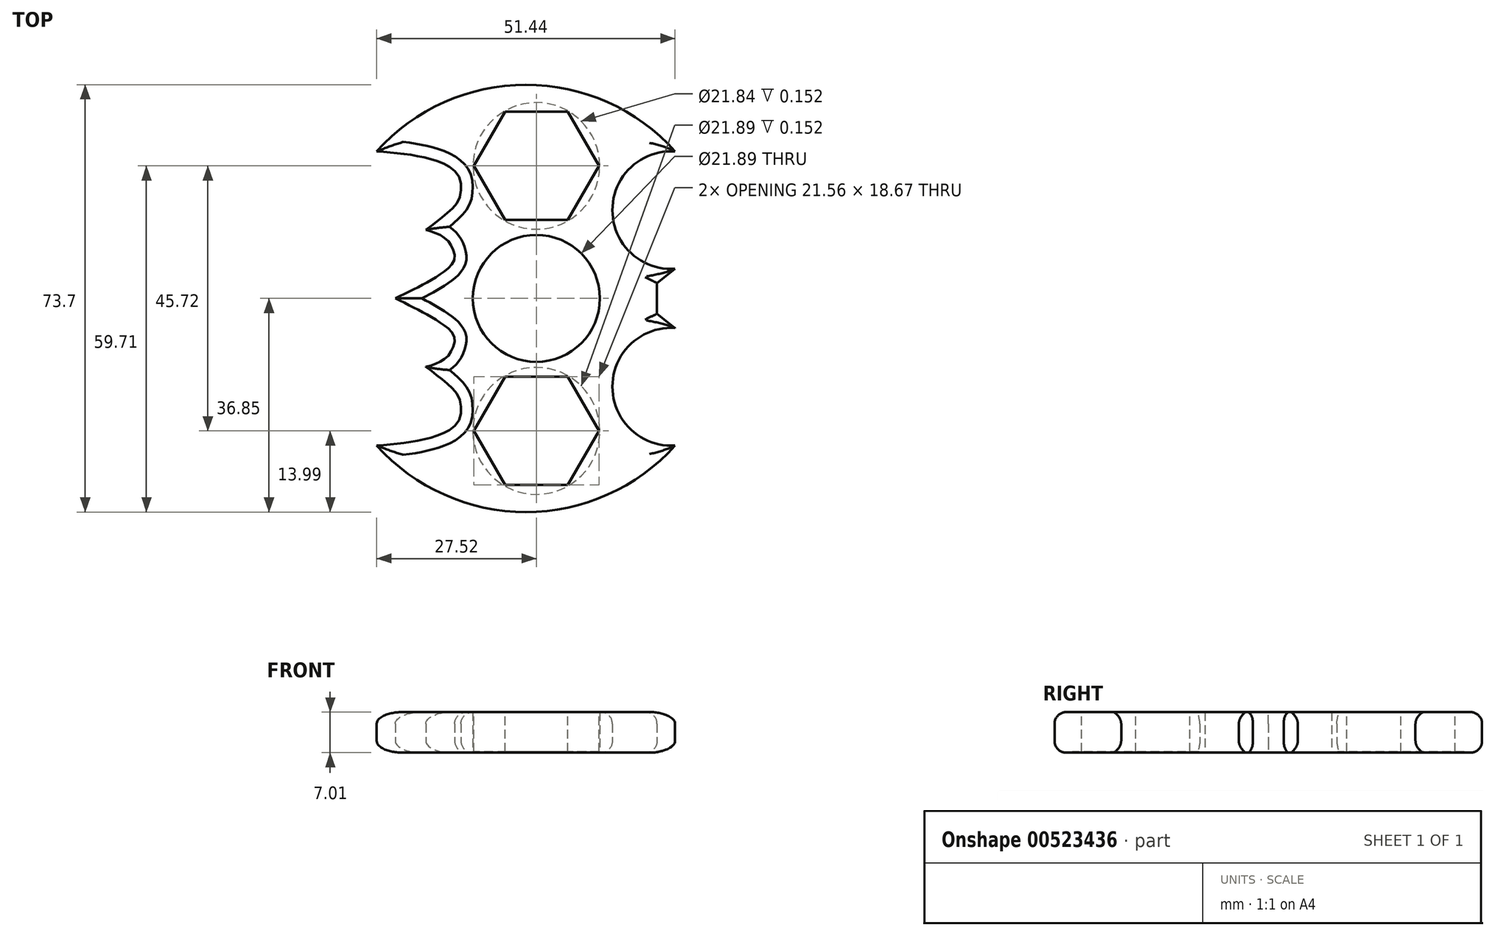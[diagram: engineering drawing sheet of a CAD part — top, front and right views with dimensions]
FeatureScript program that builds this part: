
annotation { "Feature Type Name" : "Feature", "Feature Type Description" : "" }
export const myFeature = defineFeature(function(context is Context, id is Id, definition is map)
    precondition{}
    {
        {
            var Q0;
            Q0=qCreatedBy(makeId("Top.planeOp"),FACE);
            var sketch = newSketch(context, id + "F0", { "sketchPlane" : qUnion([Q0])});
            skCircle(sketch, "E0.cCircle", {"center": v(0, 0) * mm, "radius": 12.7 * mm, "construction": true});
            skCircle(sketch, "E1", {"center": v(0, 0) * mm, "radius": 10.95 * mm});
            skLineSegment(sketch, "E2.bottom", {"start": v(4.8, 12.7) * mm, "end": v(-4.8, 12.7) * mm});
            skLineSegment(sketch, "E3.bottom", {"start": v(4.8, -11.43) * mm, "end": v(-4.8, -11.43) * mm});
            skLineSegment(sketch, "E4.MirrorCS", {"start": v(4.8, -76.2) * mm, "end": v(-4.8, -76.2) * mm});
            skLineSegment(sketch, "E5.MirrorCS", {"start": v(4.8, -73.66) * mm, "end": v(4.8, -76.2) * mm});
            skLineSegment(sketch, "E6.MirrorCS", {"start": v(7.33, -12.7) * mm, "end": v(-7.33, -12.7) * mm});
            skCircle(sketch, "E7.MirrorC", {"center": v(0, -22.86) * mm, "radius": 12.7 * mm, "construction": true});
            skCircle(sketch, "E8.MirrorC", {"center": v(0, -22.86) * mm, "radius": 10.95 * mm});
            skCircle(sketch, "E9.MirrorC", {"center": v(0, 22.86) * mm, "radius": 12.5 * mm, "construction": true});
            skCircle(sketch, "E10.MirrorC", {"center": v(0, 22.86) * mm, "radius": 10.92 * mm});
            skLineSegment(sketch, "E11", {"start": v(20.81, 0) * mm, "end": v(20.81, 2.65) * mm});
            skLineSegment(sketch, "E12", {"start": v(20.81, 2.65) * mm, "end": v(23.92, 5.09) * mm});
            skArc(sketch, "E13", {"start": v(23.92, 25.37) * mm, "mid": v(13.1, 15.23) * mm, "end": v(23.92, 5.09) * mm});
            skArc(sketch, "E14", {"start": v(23.92, 25.37) * mm, "mid": v(-1.8, 36.85) * mm, "end": v(-27.52, 25.37) * mm});
            skFitSpline(sketch, "E15", {"points": [v(-27.52, 25.37) * mm, v(-13.04, 18.5) * mm, v(-19.05, 11.82) * mm], "startDerivative": vector(78.47, -4.85) * mm, "endDerivative": vector(-39.75, -28.97) * mm});
            skFitSpline(sketch, "E16", {"points": [v(-19.05, 11.82) * mm, v(-14.33, 8.23) * mm, v(-24.33, 0) * mm], "startDerivative": vector(29.04, -7.57) * mm, "endDerivative": vector(-56.04, -26.66) * mm});
            skLineSegment(sketch, "E17.MirrorCS", {"start": v(20.81, 0) * mm, "end": v(20.81, -2.65) * mm});
            skLineSegment(sketch, "E18.MirrorCS", {"start": v(20.81, -2.65) * mm, "end": v(23.92, -5.09) * mm});
            skArc(sketch, "E19.MirrorCS", {"start": v(23.92, -25.37) * mm, "mid": v(13.1, -15.23) * mm, "end": v(23.92, -5.09) * mm});
            skArc(sketch, "E20.MirrorCS", {"start": v(23.92, -25.37) * mm, "mid": v(-1.8, -36.85) * mm, "end": v(-27.52, -25.37) * mm});
            skFitSpline(sketch, "E21.MirrorCS", {"points": [v(-27.52, -25.37) * mm, v(-13.04, -18.5) * mm, v(-19.05, -11.82) * mm], "startDerivative": vector(78.47, 4.85) * mm, "endDerivative": vector(-39.75, 28.97) * mm});
            skFitSpline(sketch, "E22.MirrorCS", {"points": [v(-19.05, -11.82) * mm, v(-14.33, -8.23) * mm, v(-24.33, 0) * mm], "startDerivative": vector(29.04, 7.57) * mm, "endDerivative": vector(-56.04, 26.66) * mm});
            skSolve(sketch);
        }
        {
            var Q0;
            Q0=qSketchRegion(id+"F0",true);
            var Q1;
            {var subQ1=sQuery(id+"F0.wireOp",EDGE,"E0.1");Q1=makeQuery(id+"F0.imprint","IMPRINT",FACE,{"disambiguationData":[TD([[makeQuery(id+"F0.imprint","IMPRINT",EDGE,{"derivedFrom":subQ1}),-1.0]])]});}
            extrude(context, id + "F1", {"entities" : qUnion([Q0, Q1]), "depth" : 7 * mm, "offsetDistance" : 25.4 * mm});
        }
        {
            var Q0;
            Q0=makeQuery(id+"F1.opExtrude","CAP_EDGE",EDGE,{"disambiguationData":[OSD([sQuery(id+"F0.wireOp",EDGE,"UyywlGDB-5Jgc-yo0l-qGuh-bbdJMILhEXu3")])],"isStart":true});
            var Q1;
            Q1=makeQuery(id+"F1.opExtrude","CAP_EDGE",EDGE,{"disambiguationData":[OSD([sQuery(id+"F0.wireOp",EDGE,"UyywlGDB-5Jgc-yo0l-qGuh-bbdJMILhEXu3")])],"isStart":false});
            var Q2;
            Q2=makeQuery(id+"F1.opExtrude","CAP_EDGE",EDGE,{"disambiguationData":[OSD([sQuery(id+"F0.wireOp",EDGE,"WgatU1v8-sKzI-u2eX-Sff9-52ynPzkIywBV")])],"isStart":true});
            var Q3;
            Q3=makeQuery(id+"F1.opExtrude","CAP_EDGE",EDGE,{"disambiguationData":[OSD([sQuery(id+"F0.wireOp",EDGE,"WgatU1v8-sKzI-u2eX-Sff9-52ynPzkIywBV")])],"isStart":false});
            var Q4;
            Q4=makeQuery(id+"F1.opExtrude","CAP_EDGE",EDGE,{"disambiguationData":[OSD([sQuery(id+"F0.wireOp",EDGE,"6KD2nS0l-Hg2D-HksP-1Ouw-CZn9uDxc5PTc")])],"isStart":true});
            var Q5;
            Q5=makeQuery(id+"F1.opExtrude","CAP_EDGE",EDGE,{"disambiguationData":[OSD([sQuery(id+"F0.wireOp",EDGE,"J5kapQ5n-iDyL-HHIj-PmFu-jLv0Z1pDbZps")])],"isStart":true});
            var Q6;
            Q6=makeQuery(id+"F1.opExtrude","CAP_EDGE",EDGE,{"disambiguationData":[OSD([sQuery(id+"F0.wireOp",EDGE,"J5kapQ5n-iDyL-HHIj-PmFu-jLv0Z1pDbZps")])],"isStart":false});
            var Q7;
            Q7=makeQuery(id+"F1.opExtrude","CAP_EDGE",EDGE,{"disambiguationData":[OSD([sQuery(id+"F0.wireOp",EDGE,"6KD2nS0l-Hg2D-HksP-1Ouw-CZn9uDxc5PTc")])],"isStart":false});
            var Q8;
            Q8=makeQuery(id+"F1.opExtrude","CAP_EDGE",EDGE,{"disambiguationData":[OSD([sQuery(id+"F0.wireOp",EDGE,"RGc6EknY-F7E9-4rBv-WTXc-wHNUPe1DTfrm")])],"isStart":true});
            var Q9;
            Q9=makeQuery(id+"F1.opExtrude","CAP_EDGE",EDGE,{"disambiguationData":[OSD([sQuery(id+"F0.wireOp",EDGE,"RGc6EknY-F7E9-4rBv-WTXc-wHNUPe1DTfrm")])],"isStart":false});
            var Q10;
            Q10=makeQuery(id+"F1.opExtrude","CAP_EDGE",EDGE,{"disambiguationData":[OSD([sQuery(id+"F0.wireOp",EDGE,"wNdpGod0-uiPN-bQcB-ljPU-xclPaN7TEj14")])],"isStart":false});
            var Q11;
            Q11=makeQuery(id+"F1.opExtrude","CAP_EDGE",EDGE,{"disambiguationData":[OSD([sQuery(id+"F0.wireOp",EDGE,"wNdpGod0-uiPN-bQcB-ljPU-xclPaN7TEj14")])],"isStart":true});
            var Q12;
            Q12=makeQuery(id+"F1.opExtrude","CAP_EDGE",EDGE,{"disambiguationData":[OSD([sQuery(id+"F0.wireOp",EDGE,"i4p45k76-JwoF-I5pY-E1qU-otX4NrZX3LmJ")])],"isStart":true});
            var Q13;
            Q13=makeQuery(id+"F1.opExtrude","CAP_EDGE",EDGE,{"disambiguationData":[OSD([sQuery(id+"F0.wireOp",EDGE,"i4p45k76-JwoF-I5pY-E1qU-otX4NrZX3LmJ")])],"isStart":false});
            var Q14;
            Q14=makeQuery(id+"F1.opExtrude","CAP_EDGE",EDGE,{"disambiguationData":[OSD([sQuery(id+"F0.wireOp",EDGE,"TCmziQ1A-WoUB-5TRC-2sz4-3Qv1A3Y1Nol2")])],"isStart":true});
            var Q15;
            Q15=makeQuery(id+"F1.opExtrude","CAP_EDGE",EDGE,{"disambiguationData":[OSD([sQuery(id+"F0.wireOp",EDGE,"TCmziQ1A-WoUB-5TRC-2sz4-3Qv1A3Y1Nol2")])],"isStart":false});
            var Q16;
            Q16=makeQuery(id+"F1.opExtrude","CAP_EDGE",EDGE,{"disambiguationData":[OSD([sQuery(id+"F0.wireOp",EDGE,"E14")])],"isStart":false});
            var Q17;
            Q17=makeQuery(id+"F1.opExtrude","CAP_EDGE",EDGE,{"disambiguationData":[OSD([sQuery(id+"F0.wireOp",EDGE,"E14")])],"isStart":true});
            var Q18;
            Q18=makeQuery(id+"F1.opExtrude","CAP_EDGE",EDGE,{"disambiguationData":[OSD([sQuery(id+"F0.wireOp",EDGE,"E20.MirrorCS")])],"isStart":true});
            var Q19;
            Q19=makeQuery(id+"F1.opExtrude","CAP_EDGE",EDGE,{"disambiguationData":[OSD([sQuery(id+"F0.wireOp",EDGE,"E20.MirrorCS")])],"isStart":false});
            var Q20;
            Q20=makeQuery(id+"F1.opExtrude","CAP_EDGE",EDGE,{"disambiguationData":[OSD([sQuery(id+"F0.wireOp",EDGE,"E19.MirrorCS")])],"isStart":false});
            var Q21;
            Q21=makeQuery(id+"F1.opExtrude","CAP_EDGE",EDGE,{"disambiguationData":[OSD([sQuery(id+"F0.wireOp",EDGE,"E13")])],"isStart":false});
            var Q22;
            Q22=makeQuery(id+"F1.opExtrude","CAP_EDGE",EDGE,{"disambiguationData":[OSD([sQuery(id+"F0.wireOp",EDGE,"E19.MirrorCS")])],"isStart":true});
            var Q23;
            Q23=makeQuery(id+"F1.opExtrude","CAP_EDGE",EDGE,{"disambiguationData":[OSD([sQuery(id+"F0.wireOp",EDGE,"E13")])],"isStart":true});
            var Q24;
            Q24=makeQuery(id+"F1.opExtrude","CAP_EDGE",EDGE,{"disambiguationData":[OSD([sQuery(id+"F0.wireOp",EDGE,"E11"),sQuery(id+"F0.wireOp",EDGE,"E17.MirrorCS")])],"isStart":true});
            var Q25;
            Q25=makeQuery(id+"F1.opExtrude","CAP_EDGE",EDGE,{"disambiguationData":[OSD([sQuery(id+"F0.wireOp",EDGE,"E11"),sQuery(id+"F0.wireOp",EDGE,"E17.MirrorCS")])],"isStart":false});
            var Q26;
            Q26=makeQuery(id+"F1.opExtrude","CAP_EDGE",EDGE,{"disambiguationData":[OSD([sQuery(id+"F0.wireOp",EDGE,"E12")])],"isStart":false});
            var Q27;
            Q27=makeQuery(id+"F1.opExtrude","CAP_EDGE",EDGE,{"disambiguationData":[OSD([sQuery(id+"F0.wireOp",EDGE,"E12")])],"isStart":true});
            var Q28;
            Q28=makeQuery(id+"F1.opExtrude","CAP_EDGE",EDGE,{"disambiguationData":[OSD([sQuery(id+"F0.wireOp",EDGE,"E18.MirrorCS")])],"isStart":false});
            var Q29;
            Q29=makeQuery(id+"F1.opExtrude","CAP_EDGE",EDGE,{"disambiguationData":[OSD([sQuery(id+"F0.wireOp",EDGE,"E18.MirrorCS")])],"isStart":true});
            var Q30;
            Q30=makeQuery(id+"F1.opExtrude","CAP_EDGE",EDGE,{"disambiguationData":[OSD([sQuery(id+"F0.wireOp",EDGE,"E21.MirrorCS")])],"isStart":false});
            var Q31;
            Q31=makeQuery(id+"F1.opExtrude","CAP_EDGE",EDGE,{"disambiguationData":[OSD([sQuery(id+"F0.wireOp",EDGE,"E22.MirrorCS")])],"isStart":false});
            var Q32;
            Q32=makeQuery(id+"F1.opExtrude","CAP_EDGE",EDGE,{"disambiguationData":[OSD([sQuery(id+"F0.wireOp",EDGE,"E16")])],"isStart":false});
            var Q33;
            Q33=makeQuery(id+"F1.opExtrude","CAP_EDGE",EDGE,{"disambiguationData":[OSD([sQuery(id+"F0.wireOp",EDGE,"E15")])],"isStart":false});
            var Q34;
            Q34=makeQuery(id+"F1.opExtrude","CAP_EDGE",EDGE,{"disambiguationData":[OSD([sQuery(id+"F0.wireOp",EDGE,"E15")])],"isStart":true});
            var Q35;
            Q35=makeQuery(id+"F1.opExtrude","CAP_EDGE",EDGE,{"disambiguationData":[OSD([sQuery(id+"F0.wireOp",EDGE,"E16")])],"isStart":true});
            var Q36;
            Q36=makeQuery(id+"F1.opExtrude","CAP_EDGE",EDGE,{"disambiguationData":[OSD([sQuery(id+"F0.wireOp",EDGE,"E22.MirrorCS")])],"isStart":true});
            var Q37;
            Q37=makeQuery(id+"F1.opExtrude","CAP_EDGE",EDGE,{"disambiguationData":[OSD([sQuery(id+"F0.wireOp",EDGE,"E21.MirrorCS")])],"isStart":true});
            fillet(context, id + "F2", {"entities" : qUnion([Q0, Q1, Q2, Q3, Q4, Q5, Q6, Q7, Q8, Q9, Q10, Q11, Q12, Q13, Q14, Q15, Q16, Q17, Q18, Q19, Q20, Q21, Q22, Q23, Q24, Q25, Q26, Q27, Q28, Q29, Q30, Q31, Q32, Q33, Q34, Q35, Q36, Q37]), "radius" : 2.03 * mm, "tangentPropagation" : true, "allowEdgeOverflow" : false});
        }
        {
            var Q0;
            Q0=makeQuery(id+"F1.opExtrude","CAP_FACE",FACE,{"disambiguationData":[OSD([sQuery(id+"F0.wireOp",EDGE,"E1"),sQuery(id+"F0.wireOp",EDGE,"514edc31-06ac-40e3-995b-7c1c53eea3582.MirrorCS"),sQuery(id+"F0.wireOp",EDGE,"E8.MirrorC"),sQuery(id+"F0.wireOp",EDGE,"514edc31-06ac-40e3-995b-7c1c53eea3586.MirrorCS"),sQuery(id+"F0.wireOp",EDGE,"5bda6188-825b-4b41-803b-8e19fa25ede90.MirrorCS"),sQuery(id+"F0.wireOp",EDGE,"455845eb-5c42-433d-a614-b21934a475661.MirrorCS"),sQuery(id+"F0.wireOp",EDGE,"455845eb-5c42-433d-a614-b21934a475662.MirrorCS"),sQuery(id+"F0.wireOp",EDGE,"E10.MirrorC"),sQuery(id+"F0.wireOp",EDGE,"QdPQ0PJ2-Wn2Q-TIlk-QB5f-A208rq11A3H9"),sQuery(id+"F0.wireOp",EDGE,"UyywlGDB-5Jgc-yo0l-qGuh-bbdJMILhEXu3"),sQuery(id+"F0.wireOp",EDGE,"WgatU1v8-sKzI-u2eX-Sff9-52ynPzkIywBV"),sQuery(id+"F0.wireOp",EDGE,"6KD2nS0l-Hg2D-HksP-1Ouw-CZn9uDxc5PTc"),sQuery(id+"F0.wireOp",EDGE,"J5kapQ5n-iDyL-HHIj-PmFu-jLv0Z1pDbZps")])],"isStart":false});
            var sketch = newSketch(context, id + "F3", { "sketchPlane" : qUnion([Q0])});
            skCircle(sketch, "E23.cCircle", {"center": v(0, -22.86) * mm, "radius": 9.33 * mm, "construction": true});
            skLineSegment(sketch, "E23.0", {"start": v(-5.39, -13.53) * mm, "end": v(5.39, -13.53) * mm});
            skLineSegment(sketch, "E23.1", {"start": v(5.39, -13.53) * mm, "end": v(10.78, -22.86) * mm});
            skLineSegment(sketch, "E23.2", {"start": v(10.78, -22.86) * mm, "end": v(5.39, -32.2) * mm});
            skLineSegment(sketch, "E23.3", {"start": v(5.39, -32.2) * mm, "end": v(-5.39, -32.2) * mm});
            skLineSegment(sketch, "E23.4", {"start": v(-5.39, -32.2) * mm, "end": v(-10.78, -22.86) * mm});
            skLineSegment(sketch, "E23.5", {"start": v(-10.78, -22.86) * mm, "end": v(-5.39, -13.53) * mm});
            skPoint(sketch, "E23.0.midPoint", {"position": v(0, -13.53) * mm});
            skCircle(sketch, "E24.cCircle", {"center": v(0, 22.86) * mm, "radius": 9.33 * mm, "construction": true});
            skLineSegment(sketch, "E24.0", {"start": v(-5.39, 32.2) * mm, "end": v(5.39, 32.2) * mm});
            skLineSegment(sketch, "E24.1", {"start": v(5.39, 32.2) * mm, "end": v(10.78, 22.86) * mm});
            skLineSegment(sketch, "E24.2", {"start": v(10.78, 22.86) * mm, "end": v(5.39, 13.53) * mm});
            skLineSegment(sketch, "E24.3", {"start": v(5.39, 13.53) * mm, "end": v(-5.39, 13.53) * mm});
            skLineSegment(sketch, "E24.4", {"start": v(-5.39, 13.53) * mm, "end": v(-10.78, 22.86) * mm});
            skLineSegment(sketch, "E24.5", {"start": v(-10.78, 22.86) * mm, "end": v(-5.39, 32.2) * mm});
            skPoint(sketch, "E24.0.midPoint", {"position": v(0, 32.2) * mm});
            skCircle(sketch, "E25", {"center": v(0, -22.86) * mm, "radius": 11.22 * mm});
            skCircle(sketch, "E26", {"center": v(0, 22.86) * mm, "radius": 11.25 * mm});
            skSolve(sketch);
        }
        {
            var Q0;
            Q0=makeQuery(id+"F3.imprint","IMPRINT",FACE,{"disambiguationData":[TD([[makeQuery(id+"F3.imprint","IMPRINT",EDGE,{"derivedFrom":sQuery(id+"F3.wireOp",EDGE,"E25")}),1.0]])]});
            var Q1;
            Q1=makeQuery(id+"F3.imprint","IMPRINT",FACE,{"disambiguationData":[TD([[makeQuery(id+"F3.imprint","IMPRINT",EDGE,{"derivedFrom":sQuery(id+"F3.wireOp",EDGE,"E26")}),1.0]])]});
            var Q2;
            Q2=makeQuery(id+"F3.imprint","IMPRINT",FACE,{"disambiguationData":[TD([[makeQuery(id+"F3.imprint","IMPRINT",EDGE,{"derivedFrom":sQuery(id+"F3.wireOp",EDGE,"E23.0")}),1.0]])]});
            var Q3;
            Q3=makeQuery(id+"F3.imprint","IMPRINT",FACE,{"disambiguationData":[TD([[makeQuery(id+"F3.imprint","IMPRINT",EDGE,{"derivedFrom":sQuery(id+"F3.wireOp",EDGE,"E24.0")}),1.0]])]});
            var Q4;
            {var subQ0=sQuery(id+"F3.wireOp",EDGE,"E23.5");var subQ1=makeQuery(id+"F1.opExtrude","CAP_EDGE",EDGE,{"disambiguationData":[OSD([sQuery(id+"F0.wireOp",EDGE,"E8.MirrorC")])],"isStart":false});var subQ2=makeQuery(id+"F3.imprint","INTERSECT",VERTEX,{"disambiguationData":[OD(0.0)],"derivedFrom":[subQ1,subQ0]});Q4=makeQuery(id+"F3.imprint","IMPRINT",FACE,{"disambiguationData":[TD([[makeQuery(id+"F3.imprint","IMPRINT",EDGE,{"disambiguationData":[TD([[subQ2,-1.0]])],"derivedFrom":subQ0}),1.0]])]});}
            var Q5;
            {var subQ0=sQuery(id+"F3.wireOp",EDGE,"E23.4");var subQ1=makeQuery(id+"F1.opExtrude","CAP_EDGE",EDGE,{"disambiguationData":[OSD([sQuery(id+"F0.wireOp",EDGE,"E8.MirrorC")])],"isStart":false});var subQ2=makeQuery(id+"F3.imprint","INTERSECT",VERTEX,{"disambiguationData":[OD(0.0)],"derivedFrom":[subQ1,subQ0]});Q5=makeQuery(id+"F3.imprint","IMPRINT",FACE,{"disambiguationData":[TD([[makeQuery(id+"F3.imprint","IMPRINT",EDGE,{"disambiguationData":[TD([[subQ2,-1.0]])],"derivedFrom":subQ0}),1.0]])]});}
            var Q6;
            {var subQ0=sQuery(id+"F3.wireOp",EDGE,"E23.3");var subQ1=makeQuery(id+"F1.opExtrude","CAP_EDGE",EDGE,{"disambiguationData":[OSD([sQuery(id+"F0.wireOp",EDGE,"E8.MirrorC")])],"isStart":false});var subQ2=makeQuery(id+"F3.imprint","INTERSECT",VERTEX,{"disambiguationData":[OD(0.0)],"derivedFrom":[subQ1,subQ0]});Q6=makeQuery(id+"F3.imprint","IMPRINT",FACE,{"disambiguationData":[TD([[makeQuery(id+"F3.imprint","IMPRINT",EDGE,{"disambiguationData":[TD([[subQ2,-1.0]])],"derivedFrom":subQ0}),1.0]])]});}
            var Q7;
            {var subQ0=sQuery(id+"F3.wireOp",EDGE,"E23.2");var subQ1=makeQuery(id+"F1.opExtrude","CAP_EDGE",EDGE,{"disambiguationData":[OSD([sQuery(id+"F0.wireOp",EDGE,"E8.MirrorC")])],"isStart":false});var subQ2=makeQuery(id+"F3.imprint","INTERSECT",VERTEX,{"disambiguationData":[OD(0.0)],"derivedFrom":[subQ1,subQ0]});Q7=makeQuery(id+"F3.imprint","IMPRINT",FACE,{"disambiguationData":[TD([[makeQuery(id+"F3.imprint","IMPRINT",EDGE,{"disambiguationData":[TD([[subQ2,-1.0]])],"derivedFrom":subQ0}),1.0]])]});}
            var Q8;
            {var subQ0=sQuery(id+"F3.wireOp",EDGE,"E23.1");var subQ1=makeQuery(id+"F1.opExtrude","CAP_EDGE",EDGE,{"disambiguationData":[OSD([sQuery(id+"F0.wireOp",EDGE,"E8.MirrorC")])],"isStart":false});var subQ2=makeQuery(id+"F3.imprint","INTERSECT",VERTEX,{"disambiguationData":[OD(0.0)],"derivedFrom":[subQ1,subQ0]});Q8=makeQuery(id+"F3.imprint","IMPRINT",FACE,{"disambiguationData":[TD([[makeQuery(id+"F3.imprint","IMPRINT",EDGE,{"disambiguationData":[TD([[subQ2,-1.0]])],"derivedFrom":subQ0}),1.0]])]});}
            var Q9;
            {var subQ0=sQuery(id+"F3.wireOp",EDGE,"E24.3");var subQ1=makeQuery(id+"F1.opExtrude","CAP_EDGE",EDGE,{"disambiguationData":[OSD([sQuery(id+"F0.wireOp",EDGE,"E10.MirrorC")])],"isStart":false});var subQ2=makeQuery(id+"F3.imprint","INTERSECT",VERTEX,{"disambiguationData":[OD(0.0)],"derivedFrom":[subQ1,subQ0]});Q9=makeQuery(id+"F3.imprint","IMPRINT",FACE,{"disambiguationData":[TD([[makeQuery(id+"F3.imprint","IMPRINT",EDGE,{"disambiguationData":[TD([[subQ2,-1.0]])],"derivedFrom":subQ0}),1.0]])]});}
            var Q10;
            {var subQ0=sQuery(id+"F3.wireOp",EDGE,"E24.4");var subQ1=makeQuery(id+"F1.opExtrude","CAP_EDGE",EDGE,{"disambiguationData":[OSD([sQuery(id+"F0.wireOp",EDGE,"E10.MirrorC")])],"isStart":false});var subQ2=makeQuery(id+"F3.imprint","INTERSECT",VERTEX,{"disambiguationData":[OD(0.0)],"derivedFrom":[subQ1,subQ0]});Q10=makeQuery(id+"F3.imprint","IMPRINT",FACE,{"disambiguationData":[TD([[makeQuery(id+"F3.imprint","IMPRINT",EDGE,{"disambiguationData":[TD([[subQ2,-1.0]])],"derivedFrom":subQ0}),1.0]])]});}
            var Q11;
            {var subQ0=sQuery(id+"F3.wireOp",EDGE,"E24.2");var subQ1=makeQuery(id+"F1.opExtrude","CAP_EDGE",EDGE,{"disambiguationData":[OSD([sQuery(id+"F0.wireOp",EDGE,"E10.MirrorC")])],"isStart":false});var subQ2=makeQuery(id+"F3.imprint","INTERSECT",VERTEX,{"disambiguationData":[OD(0.0)],"derivedFrom":[subQ1,subQ0]});Q11=makeQuery(id+"F3.imprint","IMPRINT",FACE,{"disambiguationData":[TD([[makeQuery(id+"F3.imprint","IMPRINT",EDGE,{"disambiguationData":[TD([[subQ2,-1.0]])],"derivedFrom":subQ0}),1.0]])]});}
            var Q12;
            {var subQ0=sQuery(id+"F3.wireOp",EDGE,"E24.1");var subQ1=makeQuery(id+"F1.opExtrude","CAP_EDGE",EDGE,{"disambiguationData":[OSD([sQuery(id+"F0.wireOp",EDGE,"E10.MirrorC")])],"isStart":false});var subQ2=makeQuery(id+"F3.imprint","INTERSECT",VERTEX,{"disambiguationData":[OD(0.0)],"derivedFrom":[subQ1,subQ0]});Q12=makeQuery(id+"F3.imprint","IMPRINT",FACE,{"disambiguationData":[TD([[makeQuery(id+"F3.imprint","IMPRINT",EDGE,{"disambiguationData":[TD([[subQ2,-1.0]])],"derivedFrom":subQ0}),1.0]])]});}
            var Q13;
            {var subQ0=sQuery(id+"F3.wireOp",EDGE,"E24.5");var subQ1=makeQuery(id+"F1.opExtrude","CAP_EDGE",EDGE,{"disambiguationData":[OSD([sQuery(id+"F0.wireOp",EDGE,"E10.MirrorC")])],"isStart":false});var subQ2=makeQuery(id+"F3.imprint","INTERSECT",VERTEX,{"disambiguationData":[OD(0.0)],"derivedFrom":[subQ1,subQ0]});Q13=makeQuery(id+"F3.imprint","IMPRINT",FACE,{"disambiguationData":[TD([[makeQuery(id+"F3.imprint","IMPRINT",EDGE,{"disambiguationData":[TD([[subQ2,-1.0]])],"derivedFrom":subQ0}),1.0]])]});}
            extrude(context, id + "F4", {"entities" : qUnion([Q0, Q1, Q2, Q3, Q4, Q5, Q6, Q7, Q8, Q9, Q10, Q11, Q12, Q13]), "operationType" : NewBodyOperationType.ADD, "depth" : -6.86 * mm});
        }
    });
